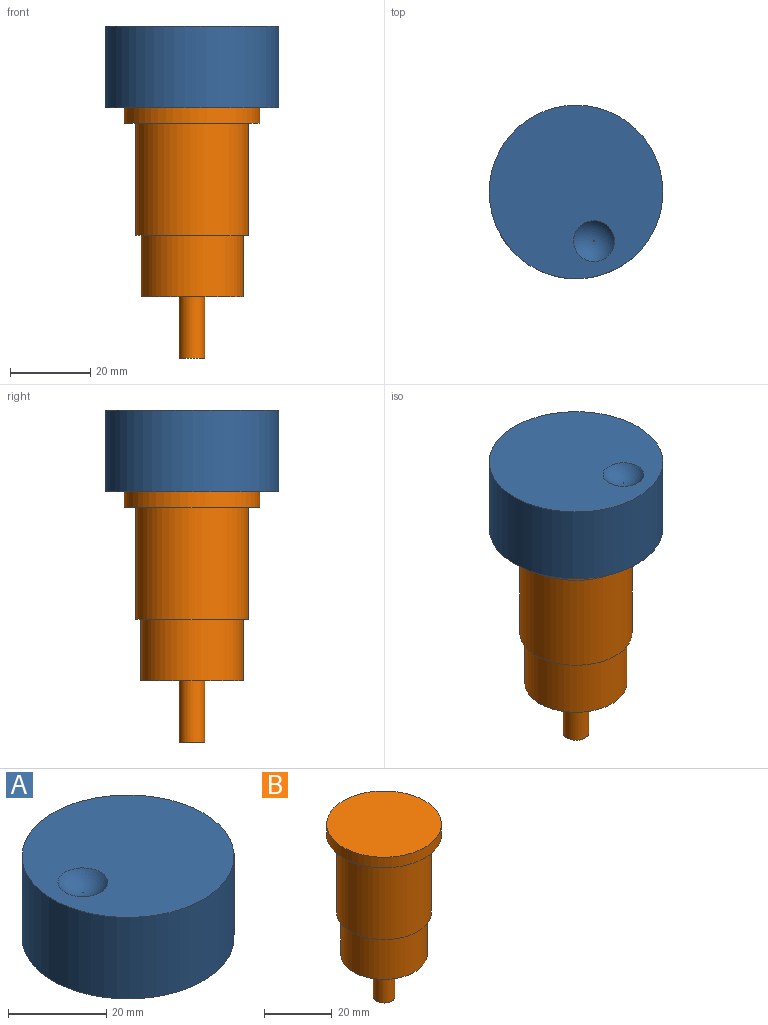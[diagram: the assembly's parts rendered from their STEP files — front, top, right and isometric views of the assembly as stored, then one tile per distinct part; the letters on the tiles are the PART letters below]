
ASSEMBLY  parts=2 mates=1
PART A: 5 faces, bbox 43.2x43.2x20.3 mm
  f0: cylinder r=21.59mm len=43.18mm, axis (0,0,-1), area 2756.5mm2, adj f1,f2
  f1: plane 43.18x43.18mm, normal (0,0,1), area 1383.3mm2, adj f0,f4
  f2: plane 43.18x43.18mm, normal (0,0,-1), area 1464.4mm2, adj f0
  f3: plane 0.13x0.13mm, normal (0,0,1), area 0mm2, adj f4
  f4: torus R=0.06mm, axis (0,0,-1), area 101.7mm2, adj f1,f3
PART B: 9 faces, bbox 33.8x33.8x62.2 mm
  f0: cylinder r=12.7mm len=25.4mm, axis (0,0,1), area 1216.1mm2, adj f3,f5
  f1: cylinder r=3.17mm len=15.24mm, axis (0,0,1), area 304mm2, adj f2,f3
  f2: plane 6.35x6.35mm, normal (0,0,-1), area 31.7mm2, adj f1
  f3: plane 25.4x25.4mm, normal (0,0,-1), area 475mm2, adj f0,f1
  f4: cylinder r=13.97mm len=27.94mm, axis (0,0,1), area 2452.5mm2, adj f5,f8
  f5: plane 27.94x27.94mm, normal (0,0,-1), area 106.4mm2, adj f0,f4
  f6: cylinder r=16.89mm len=33.78mm, axis (0,0,-1), area 404.4mm2, adj f7,f8
  f7: plane 33.78x33.78mm, normal (0,0,1), area 896.3mm2, adj f6
  f8: plane 33.78x33.78mm, normal (0,0,-1), area 283.2mm2, adj f4,f6
PLACE A rot(axis=(0,0,1),110.1deg) t=(14.1,-38.59,3.81)mm
PLACE B at identity fixed
MATE revolute A.f0 <-> B.f6  axis (0,0,-1) through (0,0,3.81)mm
